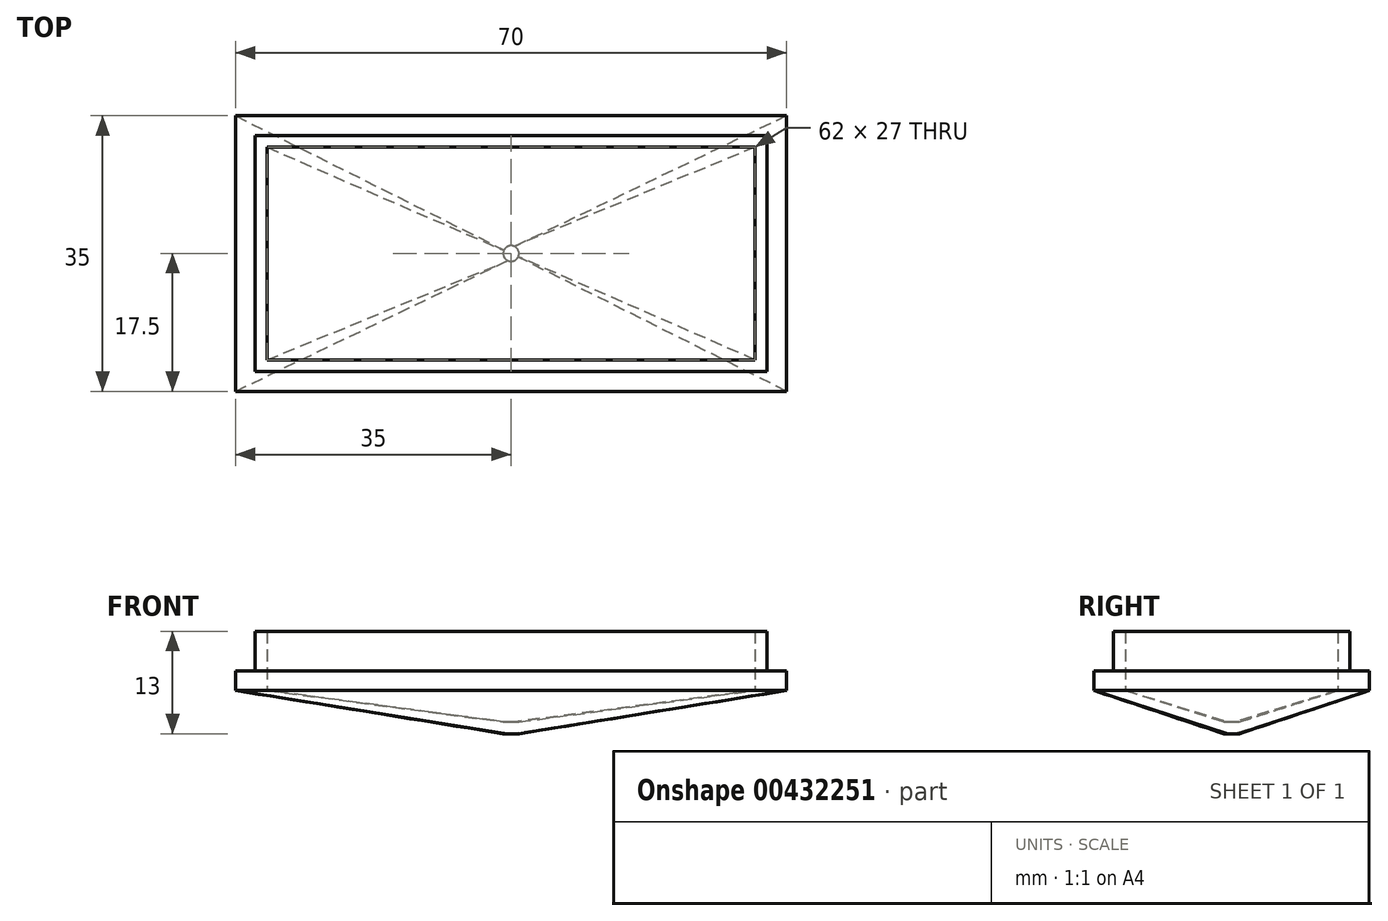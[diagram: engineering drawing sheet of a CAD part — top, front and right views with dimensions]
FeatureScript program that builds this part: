
annotation { "Feature Type Name" : "Feature", "Feature Type Description" : "" }
export const myFeature = defineFeature(function(context is Context, id is Id, definition is map)
    precondition{}
    {
        {
            var Q0;
            Q0=qCreatedBy(makeId("Top.planeOp"),FACE);
            var sketch = newSketch(context, id + "F0", { "sketchPlane" : qUnion([Q0])});
            skLineSegment(sketch, "E0.bottom", {"start": v(35, -17.5) * mm, "end": v(-35, -17.5) * mm});
            skLineSegment(sketch, "E0.top", {"start": v(35, 17.5) * mm, "end": v(-35, 17.5) * mm});
            skLineSegment(sketch, "E0.left", {"start": v(35, -17.5) * mm, "end": v(35, 17.5) * mm});
            skLineSegment(sketch, "E0.right", {"start": v(-35, -17.5) * mm, "end": v(-35, 17.5) * mm});
            skPoint(sketch, "E0.middle", {"position": v(0, 0) * mm});
            skPoint(sketch, "E1.left.end.orphan", {"position": v(32.5, 15) * mm});
            skPoint(sketch, "E2.left.end.orphan", {"position": v(31, 13.5) * mm});
            skPoint(sketch, "E2.bottom.start.orphan", {"position": v(31, -13.5) * mm});
            skPoint(sketch, "E1.bottom.start.orphan", {"position": v(32.5, -15) * mm});
            skPoint(sketch, "E2.right.end.orphan", {"position": v(-31, 13.5) * mm});
            skPoint(sketch, "E2.right.start.orphan", {"position": v(-31, -13.5) * mm});
            skPoint(sketch, "E1.right.end.orphan", {"position": v(-32.5, 15) * mm});
            skPoint(sketch, "E1.right.start.orphan", {"position": v(-32.5, -15) * mm});
            skSolve(sketch);
        }
        {
            var Q0;
            Q0=makeQuery(id+"F0.imprint","IMPRINT",FACE,{"disambiguationData":[TD([[makeQuery(id+"F0.imprint","IMPRINT",EDGE,{"derivedFrom":sQuery(id+"F0.wireOp",EDGE,"E0.bottom")}),-1.0]])]});
            extrude(context, id + "F1", {"entities" : qUnion([Q0]), "depth" : 2.5 * mm});
        }
        {
            var Q0;
            Q0=makeQuery(id+"F1.opExtrude","CAP_FACE",FACE,{"disambiguationData":[OSD([sQuery(id+"F0.wireOp",EDGE,"E0.bottom"),sQuery(id+"F0.wireOp",EDGE,"E0.top"),sQuery(id+"F0.wireOp",EDGE,"E0.left"),sQuery(id+"F0.wireOp",EDGE,"E0.right")])],"isStart":false});
            var sketch = newSketch(context, id + "F2", { "sketchPlane" : qUnion([Q0])});
            skLineSegment(sketch, "E3.bottom", {"start": v(31, -13.5) * mm, "end": v(-31, -13.5) * mm});
            skLineSegment(sketch, "E3.top", {"start": v(31, 13.5) * mm, "end": v(-31, 13.5) * mm});
            skLineSegment(sketch, "E3.left", {"start": v(31, -13.5) * mm, "end": v(31, 13.5) * mm});
            skLineSegment(sketch, "E3.right", {"start": v(-31, -13.5) * mm, "end": v(-31, 13.5) * mm});
            skPoint(sketch, "E3.middle", {"position": v(0, 0) * mm});
            skLineSegment(sketch, "E4.bottom", {"start": v(32.5, -15) * mm, "end": v(-32.5, -15) * mm});
            skLineSegment(sketch, "E4.top", {"start": v(32.5, 15) * mm, "end": v(-32.5, 15) * mm});
            skLineSegment(sketch, "E4.left", {"start": v(32.5, -15) * mm, "end": v(32.5, 15) * mm});
            skLineSegment(sketch, "E4.right", {"start": v(-32.5, -15) * mm, "end": v(-32.5, 15) * mm});
            skSolve(sketch);
        }
        {
            var Q0;
            Q0=makeQuery(id+"F2.imprint","IMPRINT",FACE,{"disambiguationData":[TD([[makeQuery(id+"F2.imprint","IMPRINT",EDGE,{"derivedFrom":sQuery(id+"F2.wireOp",EDGE,"E3.bottom")}),1.0]])]});
            extrude(context, id + "F3", {"entities" : qUnion([Q0]), "operationType" : NewBodyOperationType.ADD, "depth" : 5 * mm});
        }
        {
            var Q0;
            Q0=qCreatedBy(makeId("Right.planeOp"),FACE);
            var sketch = newSketch(context, id + "F4", { "sketchPlane" : qUnion([Q0])});
            skLineSegment(sketch, "E5", {"start": v(0, -0.75) * mm, "end": v(0, -25.75) * mm});
            skSolve(sketch);
        }
        {
            var Q0;
            Q0=makeQuery(id+"F3.boolean.opBoolean","SPLIT",FACE,{"disambiguationData":[TD([makeQuery(id+"F3.opExtrude","SWEPT_FACE",FACE,{"disambiguationData":[OSD([sQuery(id+"F2.wireOp",EDGE,"E3.bottom")])]})])],"derivedFrom":makeQuery(id+"F1.opExtrude","CAP_FACE",FACE,{"disambiguationData":[OSD([sQuery(id+"F0.wireOp",EDGE,"E0.bottom"),sQuery(id+"F0.wireOp",EDGE,"E0.top"),sQuery(id+"F0.wireOp",EDGE,"E0.left"),sQuery(id+"F0.wireOp",EDGE,"E0.right")])],"isStart":false})});
            extrude(context, id + "F5", {"entities" : qUnion([Q0]), "operationType" : NewBodyOperationType.REMOVE, "endBound" : BoundingType.UP_TO_NEXT, "oppositeDirection" : true, "depth" : 25 * mm});
        }
        {
            var Q0;
            Q0=qCreatedBy(makeId("Top.planeOp"),FACE);
            cPlane(context, id + "F6", {"entities" : qUnion([Q0]), "cplaneType" : CPlaneType.OFFSET, "offset" : 4 * mm, "oppositeDirection" : true, "width" : 150 * mm, "height" : 150 * mm});
        }
        {
            var Q0;
            Q0=qCreatedBy(id+"F6.planeOp",FACE);
            cPlane(context, id + "F7", {"entities" : qUnion([Q0]), "cplaneType" : CPlaneType.OFFSET, "offset" : 1.5 * mm, "oppositeDirection" : true, "width" : 150 * mm, "height" : 150 * mm});
        }
        {
            var Q0;
            Q0=makeQuery(id+"F1.opExtrude","CAP_FACE",FACE,{"disambiguationData":[OSD([sQuery(id+"F0.wireOp",EDGE,"E0.bottom"),sQuery(id+"F0.wireOp",EDGE,"E0.top"),sQuery(id+"F0.wireOp",EDGE,"E0.left"),sQuery(id+"F0.wireOp",EDGE,"E0.right")])],"isStart":true});
            var sketch = newSketch(context, id + "F8", { "sketchPlane" : qUnion([Q0])});
            skLineSegment(sketch, "E6.bottom", {"start": v(35, -17.5) * mm, "end": v(-35, -17.5) * mm});
            skLineSegment(sketch, "E6.top", {"start": v(35, 17.5) * mm, "end": v(-35, 17.5) * mm});
            skLineSegment(sketch, "E6.left", {"start": v(35, -17.5) * mm, "end": v(35, 17.5) * mm});
            skLineSegment(sketch, "E6.right", {"start": v(-35, -17.5) * mm, "end": v(-35, 17.5) * mm});
            skPoint(sketch, "E6.middle", {"position": v(0, 0) * mm});
            skSolve(sketch);
        }
        {
            var Q0;
            Q0=qCreatedBy(id+"F6.planeOp",FACE);
            var sketch = newSketch(context, id + "F9", { "sketchPlane" : qUnion([Q0])});
            skCircle(sketch, "E7", {"center": v(0, 0) * mm, "radius": 1 * mm});
            skSolve(sketch);
        }
        {
            var Q0;
            Q0=qCreatedBy(id+"F7.planeOp",FACE);
            var sketch = newSketch(context, id + "F10", { "sketchPlane" : qUnion([Q0])});
            skCircle(sketch, "E8", {"center": v(0, 0) * mm, "radius": 1 * mm});
            skSolve(sketch);
        }
        {
            var Q0;
            Q0=makeQuery(id+"F8.imprint","IMPRINT",FACE,{"disambiguationData":[TD([[makeQuery(id+"F8.imprint","IMPRINT",EDGE,{"derivedFrom":sQuery(id+"F8.wireOp",EDGE,"E6.bottom")}),-1.0]])]});
            var sketch = newSketch(context, id + "F11", { "sketchPlane" : qUnion([Q0])});
            skLineSegment(sketch, "E9.bottom", {"start": v(31, 13.5) * mm, "end": v(-31, 13.5) * mm});
            skLineSegment(sketch, "E9.top", {"start": v(31, -13.5) * mm, "end": v(-31, -13.5) * mm});
            skLineSegment(sketch, "E9.left", {"start": v(31, 13.5) * mm, "end": v(31, -13.5) * mm});
            skLineSegment(sketch, "E9.right", {"start": v(-31, 13.5) * mm, "end": v(-31, -13.5) * mm});
            skPoint(sketch, "E9.middle", {"position": v(0, 0) * mm});
            skSolve(sketch);
        }
        {
            var Q0;
            Q0 = qSketchRegion(id + "F11", true);
            var Q1;
            Q1=makeQuery(id+"F9.imprint","IMPRINT",FACE,{"disambiguationData":[TD([[makeQuery(id+"F9.imprint","IMPRINT",EDGE,{"derivedFrom":sQuery(id+"F9.wireOp",EDGE,"E7")}),1.0]])]});
            loft(context, id + "F12", {"sheetProfilesArray" : [{ "sheetProfileEntities" : qUnion([Q0]) }, { "sheetProfileEntities" : qUnion([Q1]) }]});
        }
        {
            var Q0;
            Q0 = qSketchRegion(id + "F8", true);
            var Q1;
            Q1=makeQuery(id+"F10.imprint","IMPRINT",FACE,{"disambiguationData":[TD([[makeQuery(id+"F10.imprint","IMPRINT",EDGE,{"derivedFrom":sQuery(id+"F10.wireOp",EDGE,"E8")}),1.0]])]});
            loft(context, id + "F13", {"sheetProfilesArray" : [{ "sheetProfileEntities" : qUnion([Q0]) }, { "sheetProfileEntities" : qUnion([Q1]) }]});
        }
    });
